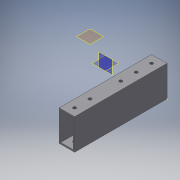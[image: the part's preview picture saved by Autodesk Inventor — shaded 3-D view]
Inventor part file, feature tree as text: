
AUTODESK INVENTOR PART (.ipt)
format: ipt  version: 2018 (Build 220112000, 112)  size: 145,920 bytes
history: native  units: in
note: dims shown in document units (in); Inventor stores cm internally (conversion verified against a paired STEP export)
features: plane x4, sketch x4, extrude x3
ambient origin geometry x8: Origin, YZ Plane, XZ Plane, XY Plane, X Axis, Y Axis, Z Axis, Center Point
bodies: Body1 (feature_tree)
feature tree (11):
  plane  "Work Plane1"
  extrude  "Extrusion13"  Depth=1.0in
  plane  "Work Plane4"
  plane  "Work Plane3"
  extrude  "Extrusion16"  Depth=0.1in
  plane  "Work Plane2"
  extrude  "Extrusion20"  Depth=0.1in
  sketch  "Sketch25"  dims[d59=0.1in d60=6.0in d61=0.0in d71=0.5in d72=0.5in d73=0.5in d74=0.2031in d75=0.2031in d76=0.2031in d77=0.5in d78=0.5in d79=0.2031in d80=0.2031in d81=0.5in d82=1.0in d83=1.0in d84=1.0in d85=1.0in d86=3.0in d87=0.0in d112=0.5in d113=1.0in d114=0.2031in d115=0.2031in d116=0.5in d117=0.5in d118=2.0in d119=0.0in]
  sketch  "Sketch16"  dims[d48=0.1in d54=1.0in]
  sketch  "Sketch20"  dims[d55=2.0in d56=0.1in]
  sketch  "Sketch24"  dims[d57=0.1in d58=0.1in]
